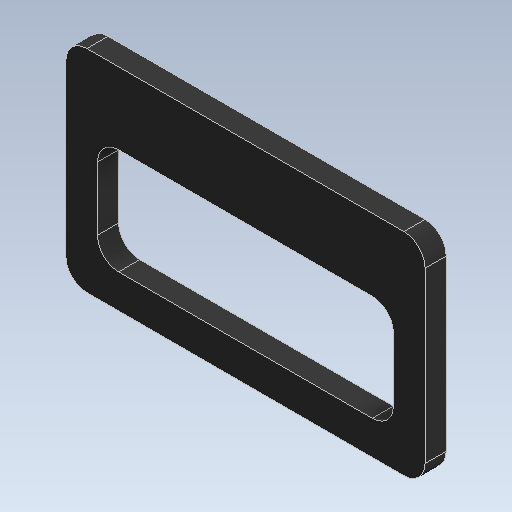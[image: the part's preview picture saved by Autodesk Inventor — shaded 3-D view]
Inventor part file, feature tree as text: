
AUTODESK INVENTOR PART (.ipt)
format: ipt  version: 2021 (Build 250183000, 183)  size: 126,464 bytes
history: native  units: mm
features: fillet x2, extrude x1, sketch x1
ambient origin geometry x8: Origin, YZ Plane, XZ Plane, XY Plane, X Axis, Y Axis, Z Axis, Center Point
bodies: Solid1 (feature_tree)
feature tree (4):
  extrude  "Extrusion1"  Depth=17.0mm
  fillet  "Fillet1"  Radius=4.1mm
  fillet  "Fillet2"  Radius=5.0mm
  sketch  "Sketch1"  dims[d0=10.0mm d1=17.0mm d2=4.1mm d3=5.0mm d4=14.0mm d5=1.0mm d6=0.0mm d7=1.0mm d8=1.0mm]
